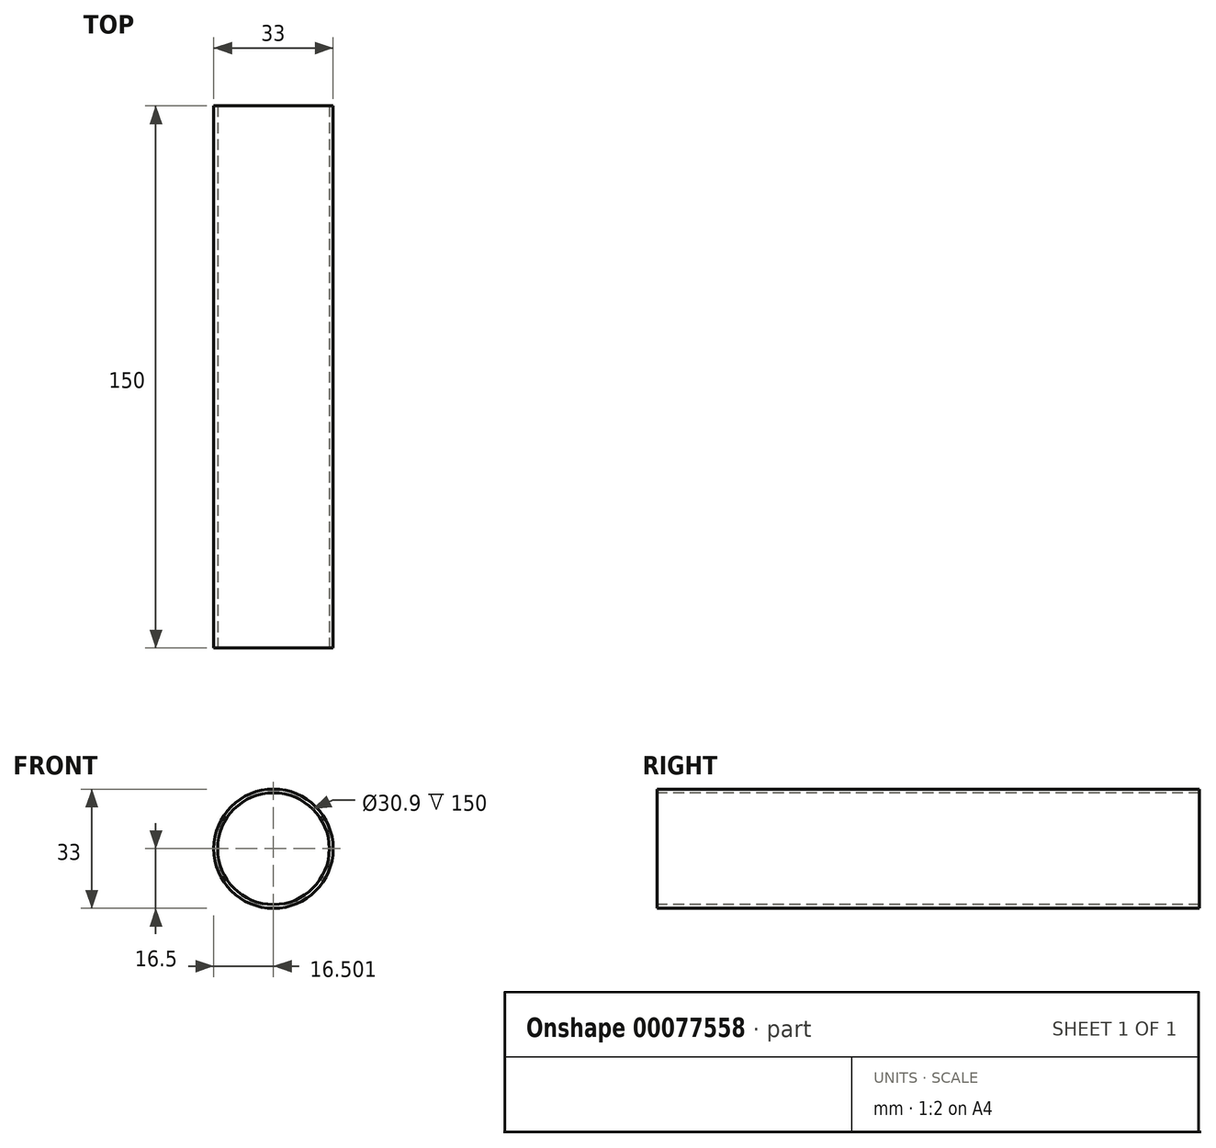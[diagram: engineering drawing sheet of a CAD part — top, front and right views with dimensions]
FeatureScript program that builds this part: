
annotation { "Feature Type Name" : "Feature", "Feature Type Description" : "" }
export const myFeature = defineFeature(function(context is Context, id is Id, definition is map)
    precondition{}
    {
        {
            var Q0;
            Q0=qCreatedBy(makeId("Front.planeOp"),FACE);
            var sketch = newSketch(context, id + "F0", { "sketchPlane" : qUnion([Q0])});
            skCircle(sketch, "E0", {"center": v(0, 0) * mm, "radius": 15 * mm});
            skCircle(sketch, "E1", {"center": v(0, 0) * mm, "radius": 14 * mm});
            skSolve(sketch);
        }
        {
            var Q0;
            Q0=sQuery(id+"F0.wireOp",EDGE,"E1");
            var Q1;
            Q1=sQuery(id+"F0.wireOp",EDGE,"E0");
            extrude(context, id + "F1", {"bodyType" : ToolBodyType.SURFACE, "surfaceEntities" : qUnion([Q0, Q1]), "depth" : 150 * mm});
        }
        {
            var Q0;
            Q0=qCreatedBy(makeId("Front.planeOp"),FACE);
            var sketch = newSketch(context, id + "F2", { "sketchPlane" : qUnion([Q0])});
            skCircle(sketch, "E2", {"center": v(-46.9, 0) * mm, "radius": 16.5 * mm});
            skCircle(sketch, "E3", {"center": v(-46.9, 0) * mm, "radius": 15.45 * mm});
            skSolve(sketch);
        }
        {
            var Q0;
            Q0 = qSketchRegion(id + "F2", true);
            var Q1;
            Q1=qCreatedBy(makeId("Front.planeOp"),FACE);
            extrude(context, id + "F3", {"entities" : qUnion([Q0]), "oppositeDirection" : true, "endBoundEntityFace" : qUnion([Q1]), "depth" : 150 * mm});
        }
    });
